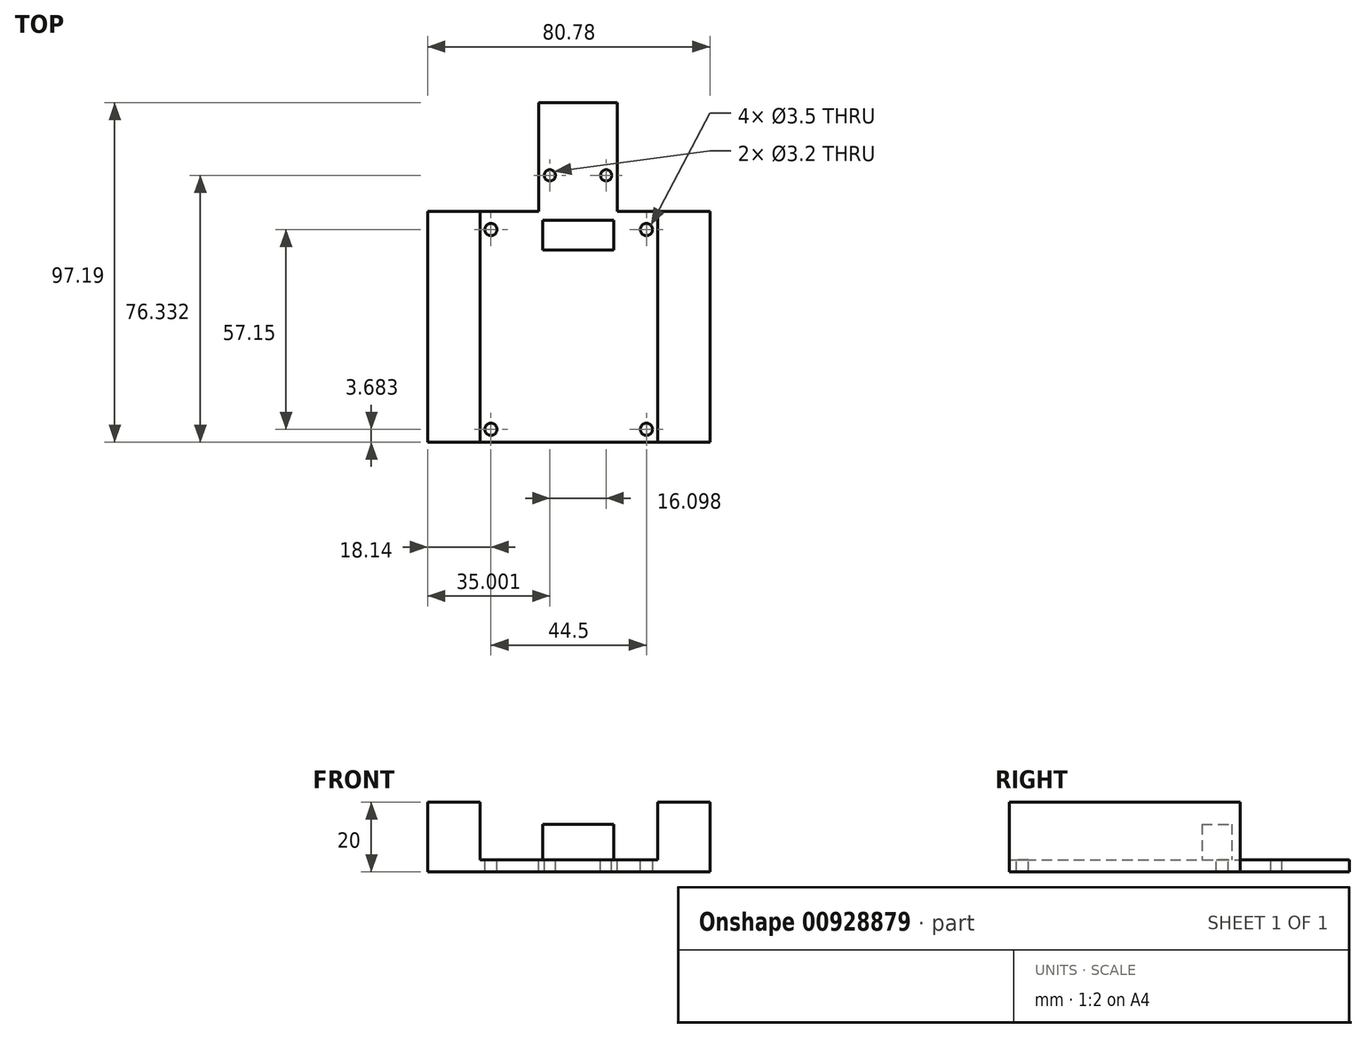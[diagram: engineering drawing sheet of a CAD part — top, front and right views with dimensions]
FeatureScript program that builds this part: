
annotation { "Feature Type Name" : "Feature", "Feature Type Description" : "" }
export const myFeature = defineFeature(function(context is Context, id is Id, definition is map)
    precondition{}
    {
        {
            var Q0;
            Q0=qCreatedBy(makeId("Top.planeOp"),FACE);
            var sketch = newSketch(context, id + "F0", { "sketchPlane" : qUnion([Q0])});
            skLineSegment(sketch, "E0.bottom", {"start": v(25.4, -33.02) * mm, "end": v(-25.4, -33.02) * mm});
            skLineSegment(sketch, "E0.top", {"start": v(25.4, 33.02) * mm, "end": v(-25.4, 33.02) * mm});
            skLineSegment(sketch, "E0.left", {"start": v(25.4, -33.02) * mm, "end": v(25.4, 33.02) * mm});
            skLineSegment(sketch, "E0.right", {"start": v(-25.4, -33.02) * mm, "end": v(-25.4, 33.02) * mm});
            skPoint(sketch, "E0.middle", {"position": v(0, 0) * mm});
            skSolve(sketch);
        }
        {
            var Q0;
            Q0=qSketchRegion(id+"F0",true);
            extrude(context, id + "F1", {"entities" : qUnion([Q0]), "depth" : 3.5 * mm, "offsetDistance" : 25 * mm});
        }
        {
            var Q0;
            Q0=makeQuery(id+"F1.opExtrude","CAP_FACE",FACE,{"disambiguationData":[OSD([sQuery(id+"F0.wireOp",EDGE,"E0.bottom"),sQuery(id+"F0.wireOp",EDGE,"E0.top"),sQuery(id+"F0.wireOp",EDGE,"E0.left"),sQuery(id+"F0.wireOp",EDGE,"E0.right")])],"isStart":false});
            var sketch = newSketch(context, id + "F2", { "sketchPlane" : qUnion([Q0])});
            skCircle(sketch, "E1", {"center": v(-22.25, 27.81) * mm, "radius": 1.75 * mm});
            skCircle(sketch, "E2", {"center": v(-22.25, -29.34) * mm, "radius": 1.75 * mm});
            skCircle(sketch, "E3", {"center": v(22.25, 27.81) * mm, "radius": 1.75 * mm});
            skCircle(sketch, "E4", {"center": v(22.25, -29.34) * mm, "radius": 1.75 * mm});
            skLineSegment(sketch, "E5", {"start": v(-22.25, -29.34) * mm, "end": v(22.25, -29.34) * mm, "construction": true});
            skLineSegment(sketch, "E6", {"start": v(0, -0.72) * mm, "end": v(0, -29.34) * mm, "construction": true});
            skLineSegment(sketch, "E7", {"start": v(-22.25, 27.81) * mm, "end": v(22.25, 27.81) * mm, "construction": true});
            skLineSegment(sketch, "E8", {"start": v(0, -0.72) * mm, "end": v(0, 27.81) * mm, "construction": true});
            skLineSegment(sketch, "E9", {"start": v(-22.25, 27.81) * mm, "end": v(-22.25, -29.34) * mm, "construction": true});
            skSolve(sketch);
        }
        {
            var Q0;
            Q0=qSketchRegion(id+"F2",true);
            extrude(context, id + "F3", {"entities" : qUnion([Q0]), "operationType" : NewBodyOperationType.REMOVE, "oppositeDirection" : true, "depth" : 25 * mm, "offsetDistance" : 25 * mm});
        }
        {
            var Q0;
            Q0=makeQuery(id+"F1.opExtrude","CAP_FACE",FACE,{"disambiguationData":[OSD([sQuery(id+"F0.wireOp",EDGE,"E0.bottom"),sQuery(id+"F0.wireOp",EDGE,"E0.top"),sQuery(id+"F0.wireOp",EDGE,"E0.left"),sQuery(id+"F0.wireOp",EDGE,"E0.right")])],"isStart":false});
            var sketch = newSketch(context, id + "F4", { "sketchPlane" : qUnion([Q0])});
            skLineSegment(sketch, "E10", {"start": v(-7.5, 30.52) * mm, "end": v(12.82, 30.52) * mm});
            skLineSegment(sketch, "E11", {"start": v(12.82, 30.52) * mm, "end": v(12.82, 22.01) * mm});
            skLineSegment(sketch, "E12", {"start": v(12.82, 22.01) * mm, "end": v(-7.5, 22.01) * mm});
            skLineSegment(sketch, "E13", {"start": v(-7.5, 22.01) * mm, "end": v(-7.5, 30.52) * mm});
            skSolve(sketch);
        }
        {
            var Q0;
            Q0=qSketchRegion(id+"F4",true);
            extrude(context, id + "F5", {"entities" : qUnion([Q0]), "operationType" : NewBodyOperationType.ADD, "depth" : 10.16 * mm, "offsetDistance" : 25 * mm});
        }
        {
            var Q0;
            Q0=makeQuery(id+"F1.opExtrude","CAP_FACE",FACE,{"disambiguationData":[OSD([sQuery(id+"F0.wireOp",EDGE,"E0.bottom"),sQuery(id+"F0.wireOp",EDGE,"E0.top"),sQuery(id+"F0.wireOp",EDGE,"E0.left"),sQuery(id+"F0.wireOp",EDGE,"E0.right")])],"isStart":true});
            var sketch = newSketch(context, id + "F6", { "sketchPlane" : qUnion([Q0])});
            skLineSegment(sketch, "E14.bottom", {"start": v(25.4, 33.02) * mm, "end": v(40.39, 33.02) * mm});
            skLineSegment(sketch, "E14.top", {"start": v(25.4, -33.02) * mm, "end": v(40.39, -33.02) * mm});
            skLineSegment(sketch, "E14.left", {"start": v(25.4, 33.02) * mm, "end": v(25.4, -33.02) * mm});
            skLineSegment(sketch, "E14.right", {"start": v(40.39, 33.02) * mm, "end": v(40.39, -33.02) * mm});
            skLineSegment(sketch, "E15.MirrorCS", {"start": v(-25.4, 33.02) * mm, "end": v(-25.4, -33.02) * mm});
            skLineSegment(sketch, "E16.MirrorCS", {"start": v(-25.4, 33.02) * mm, "end": v(-40.39, 33.02) * mm});
            skLineSegment(sketch, "E17.MirrorCS", {"start": v(-40.39, 33.02) * mm, "end": v(-40.39, -33.02) * mm});
            skLineSegment(sketch, "E18.MirrorCS", {"start": v(-25.4, -33.02) * mm, "end": v(-40.39, -33.02) * mm});
            skSolve(sketch);
        }
        {
            var Q0;
            Q0=qSketchRegion(id+"F6",true);
            extrude(context, id + "F7", {"entities" : qUnion([Q0]), "operationType" : NewBodyOperationType.ADD, "oppositeDirection" : true, "depth" : 20 * mm, "offsetDistance" : 25 * mm});
        }
        {
            var Q0;
            Q0=makeQuery(id+"F1.opExtrude","CAP_FACE",FACE,{"disambiguationData":[OSD([sQuery(id+"F0.wireOp",EDGE,"E0.bottom"),sQuery(id+"F0.wireOp",EDGE,"E0.top"),sQuery(id+"F0.wireOp",EDGE,"E0.left"),sQuery(id+"F0.wireOp",EDGE,"E0.right")])],"isStart":false});
            var sketch = newSketch(context, id + "F8", { "sketchPlane" : qUnion([Q0])});
            skLineSegment(sketch, "E19", {"start": v(2.66, 30.52) * mm, "end": v(2.66, 64.17) * mm, "construction": true});
            skLineSegment(sketch, "E20", {"start": v(2.66, 64.17) * mm, "end": v(13.88, 64.17) * mm});
            skLineSegment(sketch, "E21", {"start": v(2.66, 64.17) * mm, "end": v(-8.56, 64.17) * mm});
            skLineSegment(sketch, "E22", {"start": v(-8.56, 64.17) * mm, "end": v(-8.56, 33.02) * mm});
            skLineSegment(sketch, "E23", {"start": v(13.88, 64.17) * mm, "end": v(13.88, 33.02) * mm});
            skLineSegment(sketch, "E24", {"start": v(-8.56, 33.02) * mm, "end": v(13.88, 33.02) * mm});
            skSolve(sketch);
        }
        {
            var Q0;
            Q0=qSketchRegion(id+"F8",true);
            var Q1;
            Q1=makeQuery(id+"F7.boolean.opBoolean","MERGE",FACE,{"derivedFrom":[makeQuery(id+"F1.opExtrude","CAP_FACE",FACE,{"disambiguationData":[OSD([sQuery(id+"F0.wireOp",EDGE,"E0.bottom"),sQuery(id+"F0.wireOp",EDGE,"E0.top"),sQuery(id+"F0.wireOp",EDGE,"E0.left"),sQuery(id+"F0.wireOp",EDGE,"E0.right")])],"isStart":true}),makeQuery(id+"F7.opExtrude","CAP_FACE",FACE,{"disambiguationData":[OSD([sQuery(id+"F6.wireOp",EDGE,"E14.bottom"),sQuery(id+"F6.wireOp",EDGE,"E14.top"),sQuery(id+"F6.wireOp",EDGE,"E14.left"),sQuery(id+"F6.wireOp",EDGE,"E14.right")])],"isStart":true}),makeQuery(id+"F7.opExtrude","CAP_FACE",FACE,{"disambiguationData":[OSD([sQuery(id+"F6.wireOp",EDGE,"E15.MirrorCS"),sQuery(id+"F6.wireOp",EDGE,"E16.MirrorCS"),sQuery(id+"F6.wireOp",EDGE,"E17.MirrorCS"),sQuery(id+"F6.wireOp",EDGE,"E18.MirrorCS")])],"isStart":true})]});
            extrude(context, id + "F9", {"entities" : qUnion([Q0]), "operationType" : NewBodyOperationType.ADD, "endBound" : BoundingType.UP_TO_SURFACE, "oppositeDirection" : true, "depth" : 25 * mm, "endBoundEntityFace" : qUnion([Q1]), "offsetDistance" : 25 * mm});
        }
        {
            var Q0;
            Q0=makeQuery(id+"F9.boolean.opBoolean","MERGE",FACE,{"derivedFrom":[makeQuery(id+"F1.opExtrude","CAP_FACE",FACE,{"disambiguationData":[OSD([sQuery(id+"F0.wireOp",EDGE,"E0.bottom"),sQuery(id+"F0.wireOp",EDGE,"E0.top"),sQuery(id+"F0.wireOp",EDGE,"E0.left"),sQuery(id+"F0.wireOp",EDGE,"E0.right")])],"isStart":false}),makeQuery(id+"F9.opExtrude","CAP_FACE",FACE,{"disambiguationData":[OSD([sQuery(id+"F8.wireOp",EDGE,"E20"),sQuery(id+"F8.wireOp",EDGE,"E21"),sQuery(id+"F8.wireOp",EDGE,"E22"),sQuery(id+"F8.wireOp",EDGE,"E23"),sQuery(id+"F8.wireOp",EDGE,"E24")])],"isStart":true})]});
            var sketch = newSketch(context, id + "F10", { "sketchPlane" : qUnion([Q0])});
            skCircle(sketch, "E25", {"center": v(-5.39, 43.31) * mm, "radius": 1.6 * mm});
            skLineSegment(sketch, "E26", {"start": v(2.66, 30.52) * mm, "end": v(2.66, 62.9) * mm, "construction": true});
            skCircle(sketch, "E27.MirrorC", {"center": v(10.7, 43.31) * mm, "radius": 1.6 * mm});
            skSolve(sketch);
        }
        {
            var Q0;
            Q0=qSketchRegion(id+"F10",true);
            var Q1;
            Q1=makeQuery(id+"F1.opExtrude","SWEPT_BODY",BODY,{"disambiguationData":[OSD([sQuery(id+"F0.wireOp",EDGE,"E0.bottom"),sQuery(id+"F0.wireOp",EDGE,"E0.top"),sQuery(id+"F0.wireOp",EDGE,"E0.left"),sQuery(id+"F0.wireOp",EDGE,"E0.right")])]});
            extrude(context, id + "F11", {"entities" : qUnion([Q0]), "operationType" : NewBodyOperationType.REMOVE, "endBound" : BoundingType.UP_TO_BODY, "oppositeDirection" : true, "depth" : 25 * mm, "endBoundEntityBody" : qUnion([Q1]), "offsetDistance" : 25 * mm});
        }
    });
